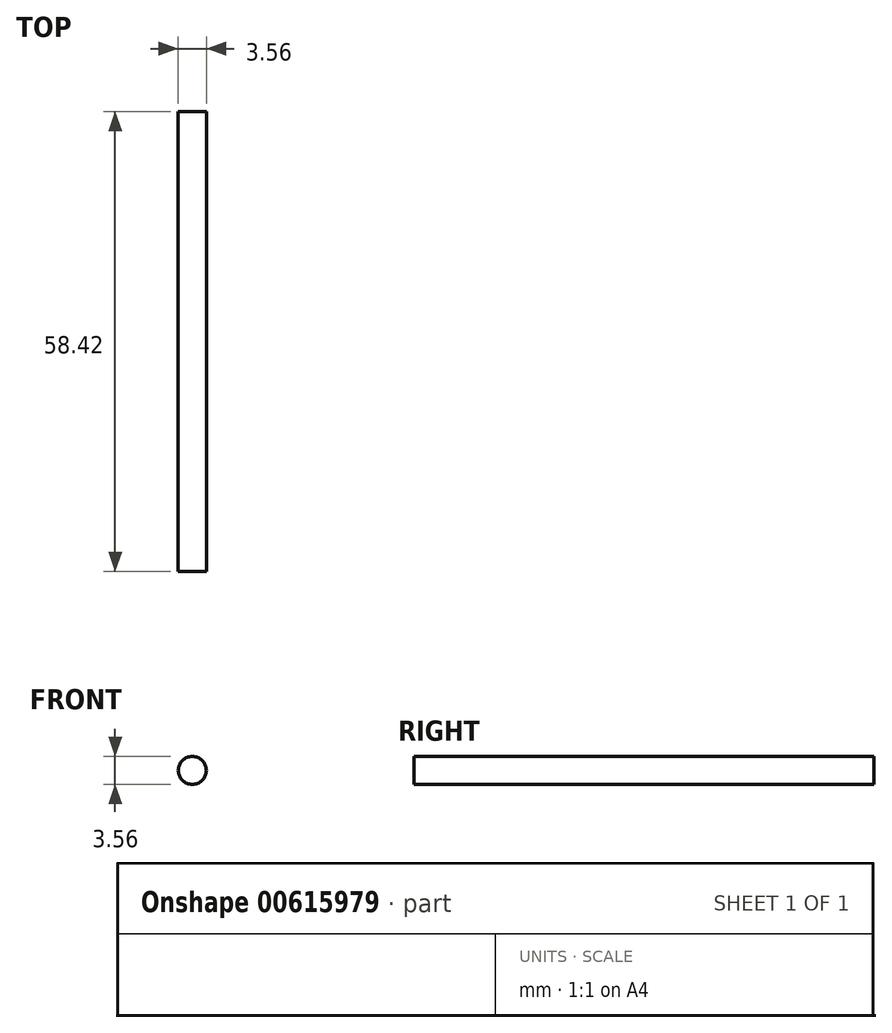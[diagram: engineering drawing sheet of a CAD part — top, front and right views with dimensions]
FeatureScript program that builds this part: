
annotation { "Feature Type Name" : "Feature", "Feature Type Description" : "" }
export const myFeature = defineFeature(function(context is Context, id is Id, definition is map)
    precondition{}
    {
        {
            var Q0;
            Q0=qCreatedBy(makeId("Front.planeOp"),FACE);
            var sketch = newSketch(context, id + "F0", { "sketchPlane" : qUnion([Q0])});
            skCircle(sketch, "E0", {"center": v(0, 0) * mm, "radius": 1.78 * mm});
            skSolve(sketch);
        }
        {
            var Q0;
            Q0=makeQuery(id+"F0.imprint","IMPRINT",FACE,{"disambiguationData":[TD([[makeQuery(id+"F0.imprint","IMPRINT",EDGE,{"derivedFrom":sQuery(id+"F0.wireOp",EDGE,"E0")}),1.0]])]});
            var Q1;
            Q1=sQuery(id+"F0.wireOp",EDGE,"E0");
            extrude(context, id + "F1", {"entities" : qUnion([Q0]), "surfaceEntities" : qUnion([Q1]), "depth" : 58.42 * mm, "offsetDistance" : 25.4 * mm});
        }
    });
